# Revit family: Gira_291600
name_source: partatom
category: Electrical Fixtures
revit_build: Autodesk Revit 2017 (Build: 20160225_1515(x64)
units: mm (PartAtom-declared; Revit-internal decimal feet)

## family parameters
Cut with Voids When Loaded = No
Host = Face
Maintain Annotation Orientation = Yes
Part Type = Normal
Room Calculation Point = No
Round Connector Dimension = Use Diameter
Shared = No

## types (1)
- Call mod. emergency set System 55
    Assembly arrangement = Basic element
    Available = No
    BIM (1) = https://media.stage.bim.site und Tasten.rfa?public/gira/36a6b08/Sys55_Komplettgerät_Schalten und Tasten.rfa
    Category = Indication element clinic-installation
    Colour = Red
    Construction = Wall mounting
    Data sheet (1) = https://katalog.gira.de
    Default Elevation = 1219 mm
    Description = Call mod.emerg.set Sys55,Call module for the emergency set,System 55,Program-neutral,Features:,- The call module is a component of the emergency set.,- The call module includes the electronics, the signal light, and the buzzer of the emergency set.,- A zero-voltage contact is provided for the duration of the emergency call.,- The visual and acoustic signal can be optionally set from continuous light   continuous tone to flashing light   emergency call using jumpers.,,Notes :,- For follow-up ordering if the emergency set should be expanded.
    GTIN = 4010337071365
    HAN = 291600
    HeinzeBIM = https://bimportal.heinze.de
    Indication = Other
    Manufacturer = Gira
    Manufacturer URL = https://www.gira.de
    Material = Other
    Material quality = Other
    Name = Call mod. emergency set System 55
    Suitable for bus connection = 2-wire
    Type of indication = Light signalling unit
    Type of power supply = Bus system
    URL = http://katalog.gira.de

## geometry (parser evidence)
native form markers: Blend x2, Sweep x10
no freeform markers — native parametric forms only
